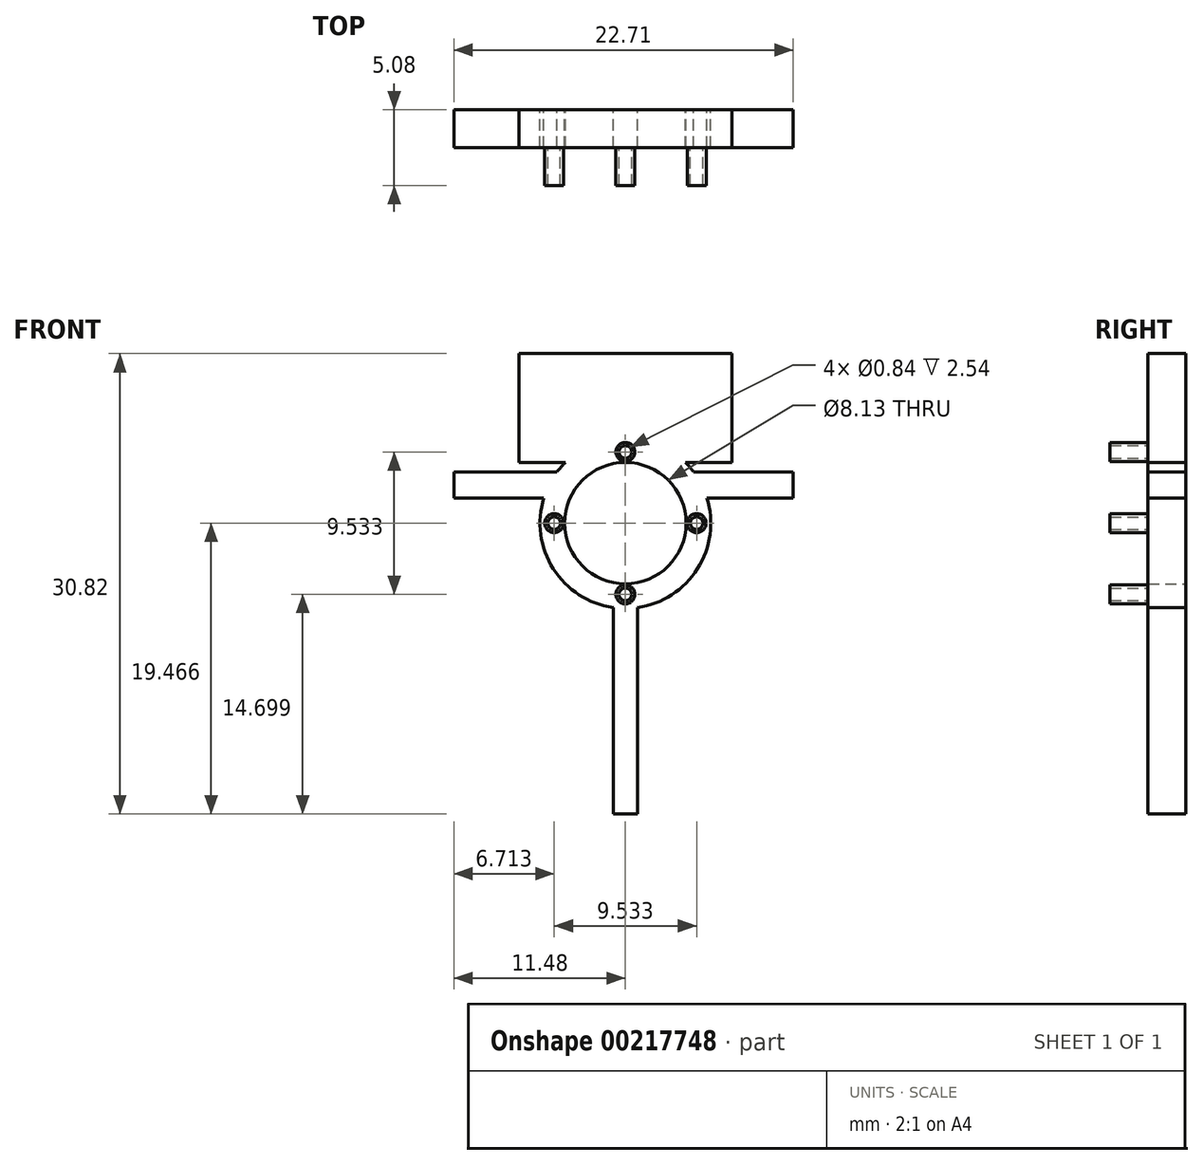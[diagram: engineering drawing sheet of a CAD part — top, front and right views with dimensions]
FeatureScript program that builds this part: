
annotation { "Feature Type Name" : "Feature", "Feature Type Description" : "" }
export const myFeature = defineFeature(function(context is Context, id is Id, definition is map)
    precondition{}
    {
        {
            var Q0;
            Q0=qCreatedBy(makeId("Front.planeOp"),FACE);
            var sketch = newSketch(context, id + "F0", { "sketchPlane" : qUnion([Q0])});
            skCircle(sketch, "E0", {"center": v(0, 23.2) * mm, "radius": 4.06 * mm});
            skCircle(sketch, "E1", {"center": v(0, 23.2) * mm, "radius": 5.72 * mm});
            skSolve(sketch);
        }
        {
            var Q0;
            Q0 = qSketchRegion(id + "F0", true);
            extrude(context, id + "F1", {"entities" : qUnion([Q0]), "depth" : 2.54 * mm});
        }
        {
            var Q0;
            Q0=makeQuery(id+"F1.opExtrude","CAP_FACE",FACE,{"disambiguationData":[OSD([sQuery(id+"F0.wireOp",EDGE,"E0"),sQuery(id+"F0.wireOp",EDGE,"E1")])],"isStart":false});
            var sketch = newSketch(context, id + "F2", { "sketchPlane" : qUnion([Q0])});
            skCircle(sketch, "E2", {"center": v(0, 27.96) * mm, "radius": 0.42 * mm});
            skCircle(sketch, "E3", {"center": v(0, 27.96) * mm, "radius": 0.64 * mm});
            skCircle(sketch, "E4.1.0", {"center": v(-4.77, 23.2) * mm, "radius": 0.64 * mm});
            skCircle(sketch, "E4.1.1", {"center": v(-4.77, 23.2) * mm, "radius": 0.42 * mm});
            skCircle(sketch, "E4.2.0", {"center": v(0, 18.43) * mm, "radius": 0.64 * mm});
            skCircle(sketch, "E4.2.1", {"center": v(0, 18.43) * mm, "radius": 0.42 * mm});
            skCircle(sketch, "E4.3.0", {"center": v(4.77, 23.2) * mm, "radius": 0.64 * mm});
            skCircle(sketch, "E4.3.1", {"center": v(4.77, 23.2) * mm, "radius": 0.42 * mm});
            skPoint(sketch, "E4.center", {"position": v(0, 23.2) * mm});
            skSolve(sketch);
        }
        {
            var Q0;
            Q0 = qSketchRegion(id + "F2", true);
            extrude(context, id + "F3", {"entities" : qUnion([Q0]), "operationType" : NewBodyOperationType.ADD, "depth" : 2.54 * mm});
        }
        {
            var Q0;
            Q0=makeQuery(id+"F1.opExtrude","CAP_FACE",FACE,{"disambiguationData":[OSD([sQuery(id+"F0.wireOp",EDGE,"E0"),sQuery(id+"F0.wireOp",EDGE,"E1")])],"isStart":true});
            var sketch = newSketch(context, id + "F4", { "sketchPlane" : qUnion([Q0])});
            skLineSegment(sketch, "E5", {"start": v(0, 27.26) * mm, "end": v(-7.13, 27.26) * mm});
            skLineSegment(sketch, "E6", {"start": v(-7.13, 27.26) * mm, "end": v(-7.13, 34.55) * mm});
            skLineSegment(sketch, "E7", {"start": v(0, 27.26) * mm, "end": v(7.13, 27.26) * mm});
            skLineSegment(sketch, "E8", {"start": v(7.13, 27.26) * mm, "end": v(7.13, 34.55) * mm});
            skLineSegment(sketch, "E9", {"start": v(7.13, 34.55) * mm, "end": v(-7.13, 34.55) * mm});
            skSolve(sketch);
        }
        {
            var Q0;
            Q0 = qSketchRegion(id + "F4", true);
            extrude(context, id + "F5", {"entities" : qUnion([Q0]), "operationType" : NewBodyOperationType.ADD, "oppositeDirection" : true, "depth" : 2.54 * mm});
        }
        {
            var Q0;
            Q0=makeQuery(id+"F1.opExtrude","CAP_FACE",FACE,{"disambiguationData":[OSD([sQuery(id+"F0.wireOp",EDGE,"E0"),sQuery(id+"F0.wireOp",EDGE,"E1")])],"isStart":true});
            var sketch = newSketch(context, id + "F6", { "sketchPlane" : qUnion([Q0])});
            skLineSegment(sketch, "E10", {"start": v(0, 18.26) * mm, "end": v(0.82, 18.26) * mm});
            skLineSegment(sketch, "E11", {"start": v(0.82, 18.26) * mm, "end": v(0.82, 3.73) * mm});
            skLineSegment(sketch, "E12", {"start": v(0, 18.26) * mm, "end": v(-0.82, 18.26) * mm});
            skLineSegment(sketch, "E13", {"start": v(-0.82, 18.26) * mm, "end": v(-0.82, 3.73) * mm});
            skLineSegment(sketch, "E14", {"start": v(-0.82, 3.73) * mm, "end": v(0.82, 3.73) * mm});
            skSolve(sketch);
        }
        {
            var Q0;
            Q0 = qSketchRegion(id + "F6", true);
            extrude(context, id + "F7", {"entities" : qUnion([Q0]), "operationType" : NewBodyOperationType.ADD, "oppositeDirection" : true, "depth" : 2.54 * mm});
        }
        {
            var Q0;
            Q0=makeQuery(id+"F1.opExtrude","CAP_FACE",FACE,{"disambiguationData":[OSD([sQuery(id+"F0.wireOp",EDGE,"E0"),sQuery(id+"F0.wireOp",EDGE,"E1")])],"isStart":true});
            var sketch = newSketch(context, id + "F8", { "sketchPlane" : qUnion([Q0])});
            skLineSegment(sketch, "E15.bottom", {"start": v(-11.23, 26.63) * mm, "end": v(-2.18, 26.63) * mm});
            skLineSegment(sketch, "E15.top", {"start": v(-11.23, 24.88) * mm, "end": v(-3.7, 24.88) * mm});
            skLineSegment(sketch, "E15.left", {"start": v(-11.23, 26.63) * mm, "end": v(-11.23, 24.88) * mm});
            skLineSegment(sketch, "E15.right", {"start": v(11.48, 26.63) * mm, "end": v(11.48, 24.88) * mm});
            skArc(sketch, "E16", {"start": v(3.7, 24.88) * mm, "mid": v(3.07, 25.86) * mm, "end": v(2.18, 26.63) * mm});
            skArc(sketch, "E17.trimOffspring", {"start": v(-2.18, 26.63) * mm, "mid": v(-3.07, 25.86) * mm, "end": v(-3.7, 24.88) * mm});
            skLineSegment(sketch, "E18.trimOffspring", {"start": v(2.18, 26.63) * mm, "end": v(11.48, 26.63) * mm});
            skLineSegment(sketch, "E19.trimOffspring", {"start": v(3.7, 24.88) * mm, "end": v(11.48, 24.88) * mm});
            skSolve(sketch);
        }
        {
            var Q0;
            Q0 = qSketchRegion(id + "F8", true);
            extrude(context, id + "F9", {"entities" : qUnion([Q0]), "operationType" : NewBodyOperationType.ADD, "oppositeDirection" : true, "depth" : 2.54 * mm});
        }
    });
